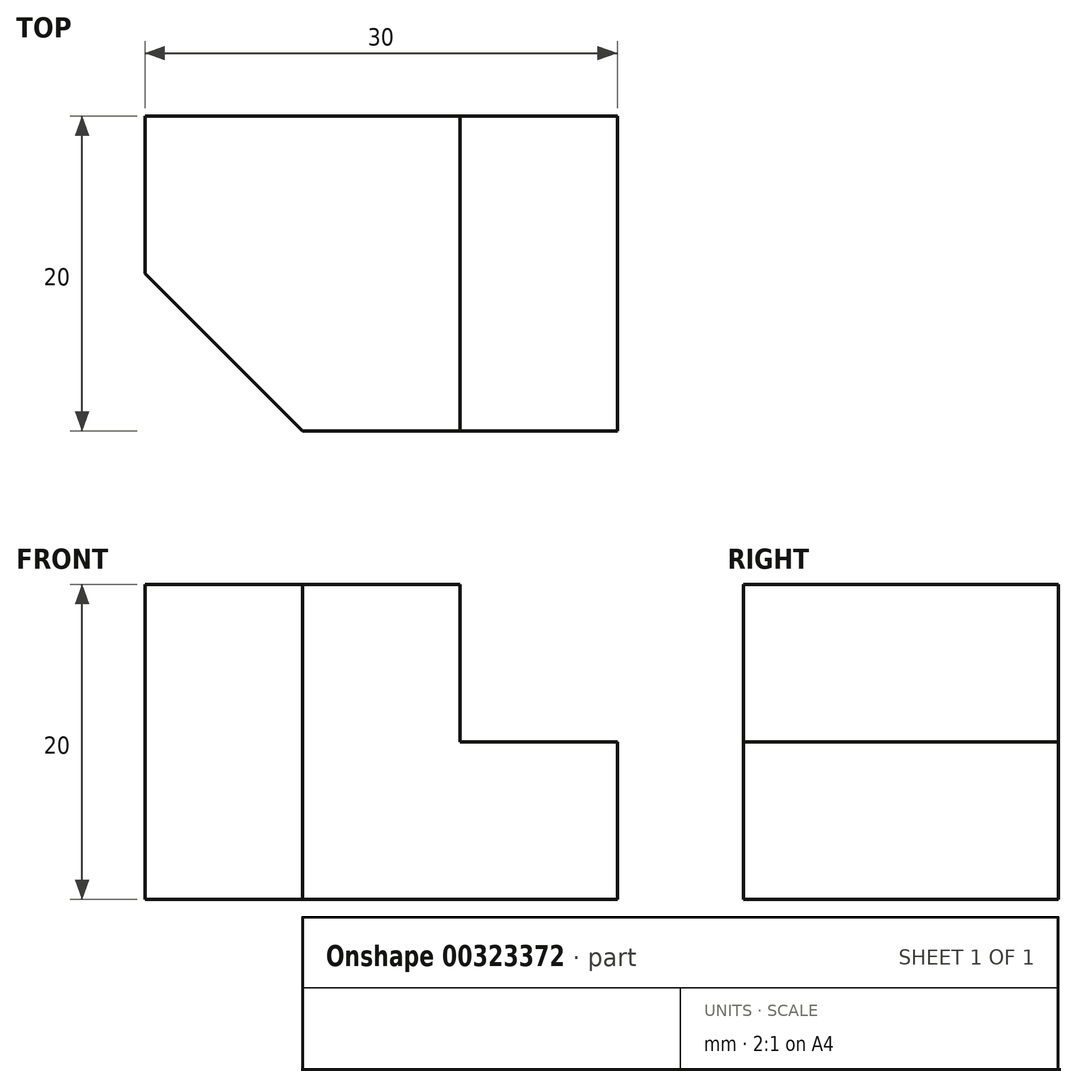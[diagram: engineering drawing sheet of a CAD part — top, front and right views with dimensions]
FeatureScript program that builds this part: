
annotation { "Feature Type Name" : "Feature", "Feature Type Description" : "" }
export const myFeature = defineFeature(function(context is Context, id is Id, definition is map)
    precondition{}
    {
        {
            var Q0;
            Q0=qCreatedBy(makeId("Front.planeOp"),FACE);
            var sketch = newSketch(context, id + "F0", { "sketchPlane" : qUnion([Q0])});
            skLineSegment(sketch, "E0", {"start": v(0, 0) * mm, "end": v(0, 20) * mm});
            skLineSegment(sketch, "E1", {"start": v(0, 20) * mm, "end": v(20, 20) * mm});
            skLineSegment(sketch, "E2", {"start": v(20, 20) * mm, "end": v(20, 10) * mm});
            skLineSegment(sketch, "E3", {"start": v(20, 10) * mm, "end": v(30, 10) * mm});
            skLineSegment(sketch, "E4", {"start": v(30, 10) * mm, "end": v(30, 0) * mm});
            skLineSegment(sketch, "E5", {"start": v(30, 0) * mm, "end": v(0, 0) * mm});
            skSolve(sketch);
        }
        {
            var Q0;
            Q0 = qSketchRegion(id + "F0", true);
            extrude(context, id + "F1", {"entities" : qUnion([Q0]), "depth" : 20 * mm});
        }
        {
            var Q0;
            Q0=qCreatedBy(makeId("Top.planeOp"),FACE);
            var sketch = newSketch(context, id + "F2", { "sketchPlane" : qUnion([Q0])});
            skLineSegment(sketch, "E6", {"start": v(0, -10) * mm, "end": v(10, -20) * mm});
            skLineSegment(sketch, "E7", {"start": v(10, -20) * mm, "end": v(0, -20) * mm});
            skLineSegment(sketch, "E8", {"start": v(0, -20) * mm, "end": v(0, -10) * mm});
            skSolve(sketch);
        }
        {
            var Q0;
            Q0 = qSketchRegion(id + "F2", true);
            extrude(context, id + "F3", {"entities" : qUnion([Q0]), "operationType" : NewBodyOperationType.REMOVE, "endBound" : BoundingType.THROUGH_ALL, "depth" : 25 * mm});
        }
    });
